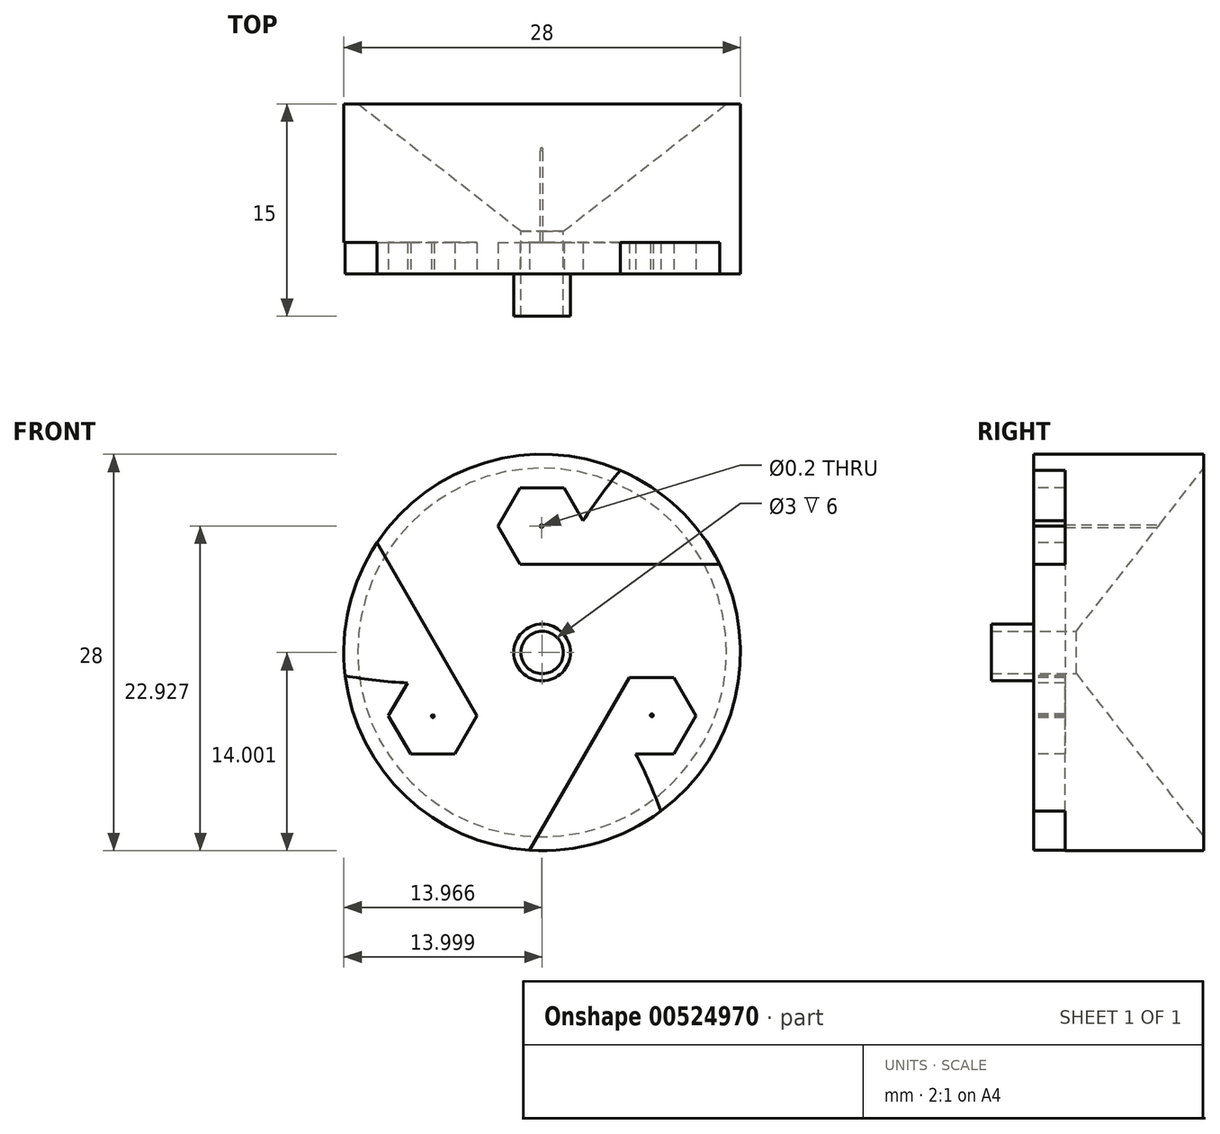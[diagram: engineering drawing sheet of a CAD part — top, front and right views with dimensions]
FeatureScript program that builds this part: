
annotation { "Feature Type Name" : "Feature", "Feature Type Description" : "" }
export const myFeature = defineFeature(function(context is Context, id is Id, definition is map)
    precondition{}
    {
        {
            var Q0;
            Q0=qCreatedBy(makeId("Front.planeOp"),FACE);
            var sketch = newSketch(context, id + "F0", { "sketchPlane" : qUnion([Q0])});
            skCircle(sketch, "E0", {"center": v(-0.72, -5.73) * mm, "radius": 14 * mm});
            skArc(sketch, "E1.0", {"start": v(4.8, 7.14) * mm, "mid": v(3.43, 5.4) * mm, "end": v(2.17, 3.58) * mm});
            skLineSegment(sketch, "E1.1", {"start": v(0.84, 5.9) * mm, "end": v(2.17, 3.58) * mm});
            skLineSegment(sketch, "E1.2", {"start": v(-2.28, 5.9) * mm, "end": v(0.84, 5.9) * mm});
            skLineSegment(sketch, "E1.4", {"start": v(11.82, 0.5) * mm, "end": v(-2.28, 0.5) * mm});
            skLineSegment(sketch, "E1.5", {"start": v(-2.28, 0.5) * mm, "end": v(-3.84, 3.2) * mm});
            skLineSegment(sketch, "E1.6", {"start": v(-3.84, 3.2) * mm, "end": v(-2.28, 5.9) * mm});
            skCircle(sketch, "E2", {"center": v(-0.72, -5.73) * mm, "radius": 1.5 * mm});
            skCircle(sketch, "E3", {"center": v(-0.72, -5.73) * mm, "radius": 2 * mm});
            skCircle(sketch, "E4", {"center": v(-0.72, -5.73) * mm, "radius": 8.93 * mm, "construction": true});
            skCircle(sketch, "E5", {"center": v(-0.75, 3.2) * mm, "radius": 0.1 * mm});
            skSolve(sketch);
        }
        {
            var Q0;
            {var subQ0=sQuery(id+"F0.wireOp",EDGE,"E1.0");Q0=makeQuery(id+"F0.imprint","IMPRINT",FACE,{"disambiguationData":[TD([[makeQuery(id+"F0.imprint","IMPRINT",EDGE,{"derivedFrom":subQ0}),-1.0]])]});}
            var Q1;
            {var subQ0=sQuery(id+"F0.wireOp",EDGE,"E1.0");Q1=makeQuery(id+"F0.imprint","IMPRINT",FACE,{"disambiguationData":[TD([[makeQuery(id+"F0.imprint","IMPRINT",EDGE,{"derivedFrom":subQ0}),1.0]])]});}
            extrude(context, id + "F1", {"entities" : qUnion([Q0, Q1]), "depth" : 12 * mm, "offsetDistance" : 25 * mm});
        }
        {
            var Q0;
            Q0=makeQuery(id+"F0.imprint","IMPRINT",FACE,{"disambiguationData":[TD([[makeQuery(id+"F0.imprint","IMPRINT",EDGE,{"derivedFrom":sQuery(id+"F0.wireOp",EDGE,"E2")}),-1.0]])]});
            extrude(context, id + "F2", {"entities" : qUnion([Q0]), "operationType" : NewBodyOperationType.ADD, "depth" : 15 * mm, "offsetDistance" : 25 * mm});
        }
        {
            var Q0;
            Q0=makeQuery(id+"F2.opExtrude","CAP_EDGE",EDGE,{"disambiguationData":[OSD([sQuery(id+"F0.wireOp",EDGE,"E2")])],"isStart":true});
            chamfer(context, id + "F3", {"entities" : qUnion([Q0]), "chamferType" : ChamferType.OFFSET_ANGLE, "width" : 9 * mm, "oppositeDirection" : true, "angle" : 52 * degree, "tangentPropagation" : true});
        }
        {
            var Q0;
            Q0=makeQuery(id+"F1.opExtrude","CAP_FACE",FACE,{"disambiguationData":[OSD([sQuery(id+"F0.wireOp",EDGE,"E0"),sQuery(id+"F0.wireOp",EDGE,"E3")])],"isStart":false});
            var sketch = newSketch(context, id + "F4", { "sketchPlane" : qUnion([Q0])});
            skLineSegment(sketch, "E6.0", {"start": v(11.82, 0.5) * mm, "end": v(-2.28, 0.5) * mm});
            skLineSegment(sketch, "E6.1", {"start": v(-2.28, 0.5) * mm, "end": v(-3.84, 3.2) * mm});
            skLineSegment(sketch, "E6.2", {"start": v(-3.84, 3.2) * mm, "end": v(-2.28, 5.9) * mm});
            skLineSegment(sketch, "E6.3", {"start": v(-2.28, 5.9) * mm, "end": v(0.84, 5.9) * mm});
            skLineSegment(sketch, "E6.4", {"start": v(0.84, 5.9) * mm, "end": v(2.17, 3.58) * mm});
            skArc(sketch, "E6.5", {"start": v(4.8, 7.14) * mm, "mid": v(3.43, 5.4) * mm, "end": v(2.17, 3.58) * mm});
            skSolve(sketch);
        }
        {
            var Q0;
            {var subQ0=sQuery(id+"F4.wireOp",EDGE,"E6.0");Q0=makeQuery(id+"F4.imprint","IMPRINT",FACE,{"disambiguationData":[TD([[makeQuery(id+"F4.imprint","IMPRINT",EDGE,{"derivedFrom":subQ0}),-1.0]])]});}
            extrude(context, id + "F5", {"entities" : qUnion([Q0]), "depth" : 2 * mm, "offsetDistance" : 25 * mm});
        }
        {
            var Q0;
            Q0=makeQuery(id+"F5.opExtrude","SWEPT_BODY",BODY,{"disambiguationData":[OSD([sQuery(id+"F0.wireOp",EDGE,"E0"),sQuery(id+"F4.wireOp",EDGE,"E6.0"),sQuery(id+"F4.wireOp",EDGE,"E6.1"),sQuery(id+"F4.wireOp",EDGE,"E6.2"),sQuery(id+"F4.wireOp",EDGE,"E6.3"),sQuery(id+"F4.wireOp",EDGE,"E6.4"),sQuery(id+"F4.wireOp",EDGE,"E6.5")])]});
            var Q1;
            Q1=sQuery(id+"F0.wireOp",EDGE,"E4");
            circularPattern(context, id + "F6", {"operationType" : NewBodyOperationType.ADD, "entities" : qUnion([Q0]), "axis" : qUnion([Q1]), "angle" : 360 * degree, "instanceCount" : 3, "equalSpace" : true, "computeTransformsWithoutBuiltin" : true});
        }
        {
            var Q0;
            Q0=makeQuery(id+"F5.opExtrude","CAP_FACE",FACE,{"disambiguationData":[OSD([sQuery(id+"F0.wireOp",EDGE,"E0"),sQuery(id+"F4.wireOp",EDGE,"E6.0"),sQuery(id+"F4.wireOp",EDGE,"E6.1"),sQuery(id+"F4.wireOp",EDGE,"E6.2"),sQuery(id+"F4.wireOp",EDGE,"E6.3"),sQuery(id+"F4.wireOp",EDGE,"E6.4"),sQuery(id+"F4.wireOp",EDGE,"E6.5")])],"isStart":false});
            var Q1;
            Q1=makeQuery(id+"F6.opPattern","COPY",FACE,{"derivedFrom":makeQuery(id+"F5.opExtrude","CAP_FACE",FACE,{"disambiguationData":[OSD([sQuery(id+"F0.wireOp",EDGE,"E0"),sQuery(id+"F4.wireOp",EDGE,"E6.0"),sQuery(id+"F4.wireOp",EDGE,"E6.1"),sQuery(id+"F4.wireOp",EDGE,"E6.2"),sQuery(id+"F4.wireOp",EDGE,"E6.3"),sQuery(id+"F4.wireOp",EDGE,"E6.4"),sQuery(id+"F4.wireOp",EDGE,"E6.5")])],"isStart":false}),"instanceName":"2"});
            var Q2;
            Q2=makeQuery(id+"F6.opPattern","COPY",FACE,{"derivedFrom":makeQuery(id+"F5.opExtrude","CAP_FACE",FACE,{"disambiguationData":[OSD([sQuery(id+"F0.wireOp",EDGE,"E0"),sQuery(id+"F4.wireOp",EDGE,"E6.0"),sQuery(id+"F4.wireOp",EDGE,"E6.1"),sQuery(id+"F4.wireOp",EDGE,"E6.2"),sQuery(id+"F4.wireOp",EDGE,"E6.3"),sQuery(id+"F4.wireOp",EDGE,"E6.4"),sQuery(id+"F4.wireOp",EDGE,"E6.5")])],"isStart":false}),"instanceName":"1"});
            extrude(context, id + "F7", {"entities" : qUnion([Q0, Q1, Q2]), "operationType" : NewBodyOperationType.REMOVE, "oppositeDirection" : true, "depth" : 4.2 * mm, "offsetDistance" : 25 * mm});
        }
    });
